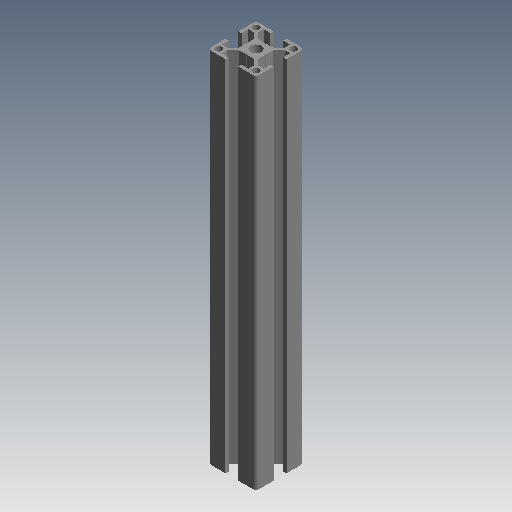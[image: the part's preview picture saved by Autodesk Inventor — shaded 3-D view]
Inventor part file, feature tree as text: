
AUTODESK INVENTOR PART (.ipt)
format: ipt  version: 2020 (Build 240168000, 168)  size: 210,432 bytes
history: native  units: mm (DEFAULTED — no unit token found)
features: other x21, sketch x3, hole x2, extrude x1, pattern_linear x1
ambient origin geometry x8: Origin, YZ Plane, XZ Plane, XY Plane, X Axis, Y Axis, Z Axis, Center Point
bodies: Solid1 (feature_tree)
feature tree (28):
  extrude  "Extrusion1"  Depth=223.0mm
  hole  "Hole1"  [1 undecoded]
  hole  "Hole2"  [1 undecoded]
  pattern_linear  "Rectangular Pattern1"  [2 undecoded]
  other  "C1_XY"
  other  "C1_YZ"
  other  "C1_ZX"
  other  "C1_X"
  other  "C1_Y"
  other  "C1_Z"
  other  "C1_Center"
  other  "to_frame_cap1_XY"
  other  "to_frame_cap1_YZ"
  other  "to_frame_cap1_ZX"
  other  "to_frame_cap1_X"
  other  "to_frame_cap1_Y"
  other  "to_frame_cap1_Z"
  other  "to_frame_cap1_Center"
  other  "to_frame_cap2_XY"
  other  "to_frame_cap2_YZ"
  other  "to_frame_cap2_ZX"
  other  "to_frame_cap2_X"
  other  "to_frame_cap2_Y"
  other  "to_frame_cap2_Z"
  other  "to_frame_cap2_Center"
  sketch  "Sketch_1"  dims[d0=223.0mm d1=0.0mm]
  sketch  "Sketch2"  dims[d2=6.8mm d3=6.0mm d4=4.0mm d5=2.0mm d6=90.0deg d7=223.0mm d8=0.0mm]
  sketch  "Sketch3"  dims[d9=4.2mm d10=6.0mm d11=4.0mm d12=2.0mm d13=90.0deg d14=223.0mm d15=0.0mm d16=20.0mm d18=23.2mm d19=20.0mm d21=23.2mm d22=0.0mm d23=0.0mm d24=0.0mm]
note: 4 required parameter values undecoded (feature->parameter linkage not recoverable at this tier; creation-order binding heuristic only, values carry confidence <= 0.55)
